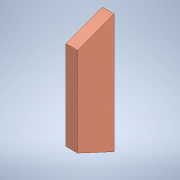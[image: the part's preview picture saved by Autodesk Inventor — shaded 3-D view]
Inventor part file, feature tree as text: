
AUTODESK INVENTOR PART (.ipt)
format: ipt  version: 2022.2 (Build 262287000, 287)  size: 108,544 bytes
history: native  units: in
note: dims shown in document units (in); Inventor stores cm internally (conversion verified against a paired STEP export)
features: extrude x1, plane x1, sketch x1
ambient origin geometry x8: Origin, YZ Plane, XZ Plane, XY Plane, X Axis, Y Axis, Z Axis, Center Point
bodies: Body1 (feature_tree)
feature tree (3):
  extrude  "Extrusion3"  TaperAngle=0.0deg  [1 undecoded]
  plane  "Work Plane2"
  sketch  "Sketch4"  dims[d15=1.75in d16=0.0in d17=0.7559in d18=-2.75in d19=0.4466in d20=5.5in d21=18.0in]
note: 1 required parameter value undecoded (feature->parameter linkage not recoverable at this tier; creation-order binding heuristic only, values carry confidence <= 0.55)
